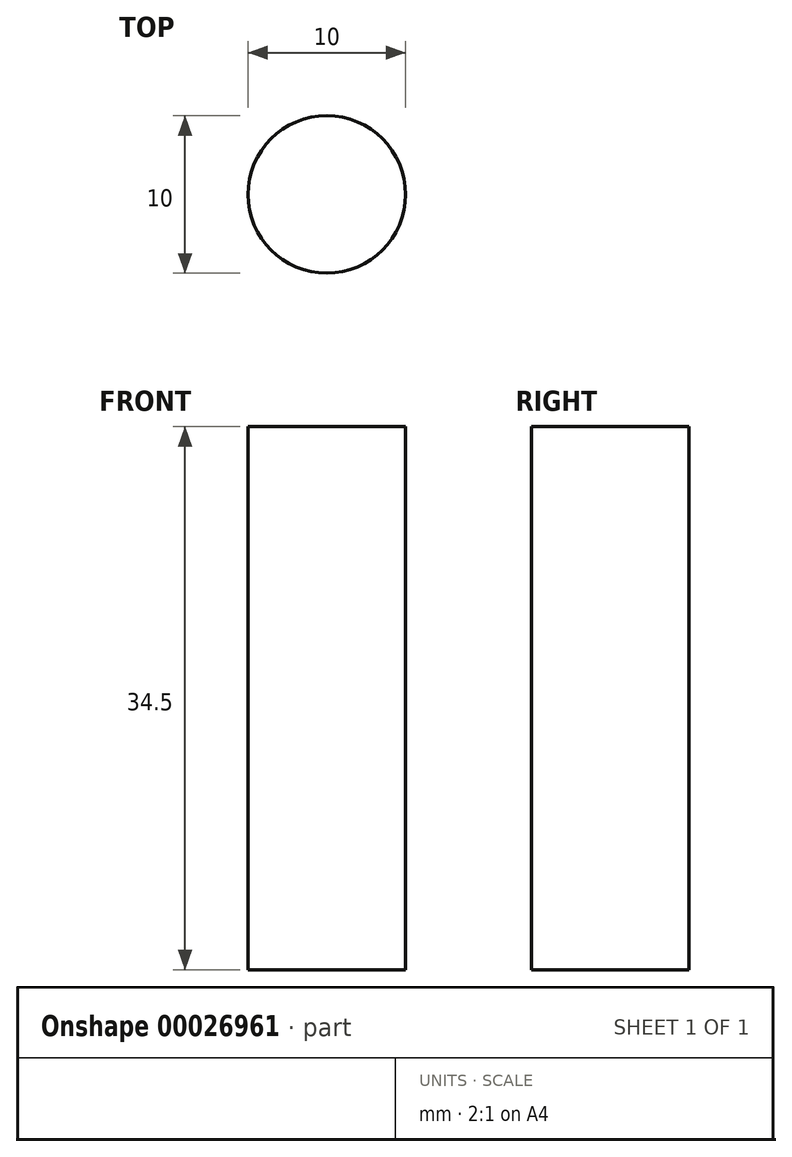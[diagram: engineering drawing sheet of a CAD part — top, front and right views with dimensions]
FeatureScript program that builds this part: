
annotation { "Feature Type Name" : "Feature", "Feature Type Description" : "" }
export const myFeature = defineFeature(function(context is Context, id is Id, definition is map)
    precondition{}
    {
        {
            var Q0;
            Q0=qCreatedBy(makeId("Top.planeOp"),FACE);
            var sketch = newSketch(context, id + "F0", { "sketchPlane" : qUnion([Q0])});
            skCircle(sketch, "E0", {"center": v(0, 0) * mm, "radius": 5 * mm});
            skSolve(sketch);
        }
        {
            var Q0;
            Q0=qSketchRegion(id+"F0",true);
            extrude(context, id + "F1", {"entities" : qUnion([Q0]), "depth" : 34.5 * mm});
        }
    });
